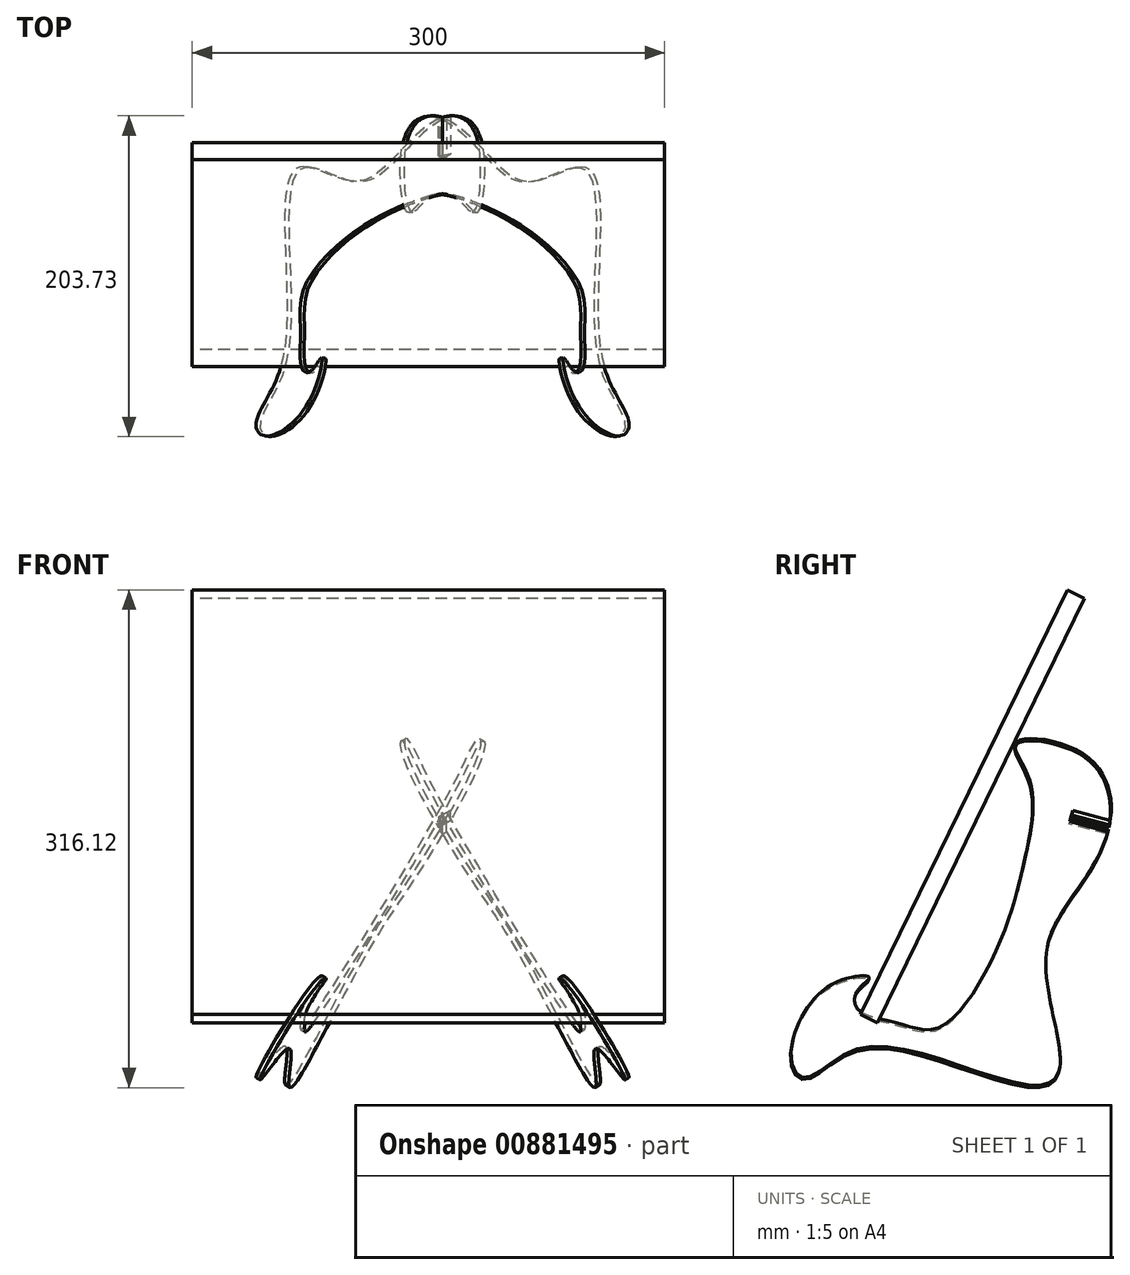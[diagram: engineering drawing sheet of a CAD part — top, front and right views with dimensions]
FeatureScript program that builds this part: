
annotation { "Feature Type Name" : "Feature", "Feature Type Description" : "" }
export const myFeature = defineFeature(function(context is Context, id is Id, definition is map)
    precondition{}
    {
        {
            var Q0;
            Q0=qCreatedBy(makeId("Front.planeOp"),FACE);
            var sketch = newSketch(context, id + "F0", { "sketchPlane" : qUnion([Q0])});
            skLineSegment(sketch, "E0.bottom", {"start": v(150, -150) * mm, "end": v(-150, -150) * mm});
            skLineSegment(sketch, "E0.top", {"start": v(150, 150) * mm, "end": v(-150, 150) * mm});
            skLineSegment(sketch, "E0.left", {"start": v(150, -150) * mm, "end": v(150, 150) * mm});
            skLineSegment(sketch, "E0.right", {"start": v(-150, -150) * mm, "end": v(-150, 150) * mm});
            skPoint(sketch, "E0.middle", {"position": v(0, 0) * mm});
            skSolve(sketch);
        }
        {
            var Q0;
            Q0 = qSketchRegion(id + "F0", true);
            extrude(context, id + "F1", {"entities" : qUnion([Q0]), "depth" : 12 * mm, "offsetDistance" : 25 * mm});
        }
        {
            var Q0;
            Q0=makeQuery(id+"F1.opExtrude","CAP_FACE",FACE,{"disambiguationData":[OSD([sQuery(id+"F0.wireOp",EDGE,"E0.bottom"),sQuery(id+"F0.wireOp",EDGE,"E0.top"),sQuery(id+"F0.wireOp",EDGE,"E0.left"),sQuery(id+"F0.wireOp",EDGE,"E0.right")])],"isStart":false});
            var sketch = newSketch(context, id + "F2", { "sketchPlane" : qUnion([Q0])});
            skLineSegment(sketch, "E1", {"start": v(-150, -150) * mm, "end": v(150, 150) * mm});
            skSolve(sketch);
        }
        {
            var Q0;
            Q0=sQuery(id+"F2.wireOp",EDGE,"E1");
            cPlane(context, id + "F3", {"entities" : qUnion([Q0]), "cplaneType" : CPlaneType.LINE_ANGLE, "offset" : 25 * mm, "angle" : 90 * degree, "width" : 150 * mm, "height" : 150 * mm});
        }
        {
            var Q0;
            Q0=makeQuery(id+"F1.opExtrude","SWEPT_BODY",BODY,{"disambiguationData":[OSD([sQuery(id+"F0.wireOp",EDGE,"E0.bottom"),sQuery(id+"F0.wireOp",EDGE,"E0.top"),sQuery(id+"F0.wireOp",EDGE,"E0.left"),sQuery(id+"F0.wireOp",EDGE,"E0.right")])]});
            var Q1;
            Q1=makeQuery(id+"F1.opExtrude","CAP_EDGE",EDGE,{"disambiguationData":[OSD([sQuery(id+"F0.wireOp",EDGE,"E0.bottom")])],"isStart":true});
            transform(context, id + "F4", {"entities" : qUnion([Q0]), "transformType" : TransformType.ROTATION, "transformAxis" : qUnion([Q1]), "angle" : 15 * degree, "makeCopy" : false});
        }
        {
            var Q0;
            Q0=qCreatedBy(makeId("Right.planeOp"),FACE);
            var sketch = newSketch(context, id + "F5", { "sketchPlane" : qUnion([Q0])});
            skFitSpline(sketch, "E2", {"points": [v(60.73, 58.65) * mm, v(102.2, 52.5) * mm, v(119.45, 8.25) * mm, v(99.15, -41.95) * mm, v(75.12, -90.56) * mm, v(79.44, -152.57) * mm, v(78.07, -183.5) * mm, v(61.93, -190.36) * mm, v(0, -172.37) * mm, v(-53.03, -169.92) * mm, v(-83.37, -190.36) * mm, v(-91.73, -177.12) * mm, v(-65.64, -123.34) * mm, v(-39.76, -115.85) * mm, v(-47.66, -126.05) * mm, v(-46.97, -140.23) * mm, v(-23.2, -148.23) * mm, v(2.9, -151.1) * mm, v(43.07, -91.63) * mm, v(63.9, -22.73) * mm, v(67.64, 32.82) * mm, v(60.73, 58.65) * mm]});
            skLineSegment(sketch, "E3", {"start": v(136.17, -190.36) * mm, "end": v(-229.05, -190.36) * mm, "construction": true});
            skSolve(sketch);
        }
        {
            var Q0;
            Q0 = qSketchRegion(id + "F5", true);
            extrude(context, id + "F6", {"entities" : qUnion([Q0]), "depth" : 3 * mm, "offsetDistance" : 25 * mm});
        }
        {
            var Q0;
            Q0=makeQuery(id+"F6.opExtrude","SWEPT_BODY",BODY,{"disambiguationData":[OSD([sQuery(id+"F5.wireOp",EDGE,"E2")])]});
            var Q1;
            Q1=makeQuery(id+"F1.opExtrude","SWEPT_EDGE",EDGE,{"disambiguationData":[OSD([sQuery(id+"F0.wireOp",EDGE,"E0.bottom"),sQuery(id+"F0.wireOp",EDGE,"E0.right")])]});
            transform(context, id + "F7", {"entities" : qUnion([Q0]), "transformType" : TransformType.ROTATION, "transformAxis" : qUnion([Q1]), "angle" : 30 * degree, "makeCopy" : false});
        }
        {
            var Q0;
            Q0=makeQuery(id+"F6.opExtrude","SWEPT_BODY",BODY,{"disambiguationData":[OSD([sQuery(id+"F5.wireOp",EDGE,"E2")])]});
            var Q1;
            Q1=qCreatedBy(makeId("Right.planeOp"),FACE);
            mirror(context, id + "F8", {"entities" : qUnion([Q0]), "mirrorPlane" : qUnion([Q1])});
        }
        {
            var Q0;
            Q0=makeQuery(id+"F8.opPattern","COPY",BODY,{"derivedFrom":makeQuery(id+"F6.opExtrude","SWEPT_BODY",BODY,{"disambiguationData":[OSD([sQuery(id+"F5.wireOp",EDGE,"E2")])]}),"instanceName":"1"});
            transform(context, id + "F9", {"entities" : qUnion([Q0]), "transformType" : TransformType.TRANSLATION_3D, "dx" : 136 * mm, "dy" : 0 * mm, "dz" : 0 * mm, "makeCopy" : false});
        }
        {
            var Q0;
            Q0=makeQuery(id+"F8.opPattern","COPY",FACE,{"derivedFrom":makeQuery(id+"F6.opExtrude","CAP_FACE",FACE,{"disambiguationData":[OSD([sQuery(id+"F5.wireOp",EDGE,"E2")])],"isStart":true}),"instanceName":"1"});
            var sketch = newSketch(context, id + "F10", { "sketchPlane" : qUnion([Q0])});
            skFitSpline(sketch, "E4", {"points": [v(41.28, -104.32) * mm, v(41.15, -105.47) * mm, v(41.02, -106.63) * mm, v(40.88, -107.78) * mm]});
            skFitSpline(sketch, "E5", {"points": [v(89.54, -119.07) * mm, v(89.78, -117.94) * mm, v(90.02, -116.81) * mm, v(90.25, -115.68) * mm]});
            skLineSegment(sketch, "E6", {"start": v(40.88, -107.78) * mm, "end": v(89.54, -119.07) * mm});
            skLineSegment(sketch, "E7", {"start": v(41.28, -104.32) * mm, "end": v(90.25, -115.68) * mm});
            skFitSpline(sketch, "E8", {"points": [v(41.28, -104.32) * mm, v(41.15, -105.47) * mm, v(41.02, -106.63) * mm, v(40.88, -107.78) * mm]});
            skFitSpline(sketch, "E9", {"points": [v(89.54, -119.07) * mm, v(89.78, -117.94) * mm, v(90.02, -116.81) * mm, v(90.25, -115.68) * mm]});
            skSolve(sketch);
        }
        {
            var Q0;
            Q0=makeQuery(id+"F8.opPattern","COPY",FACE,{"derivedFrom":makeQuery(id+"F6.opExtrude","CAP_FACE",FACE,{"disambiguationData":[OSD([sQuery(id+"F5.wireOp",EDGE,"E2")])],"isStart":false}),"instanceName":"1"});
            var sketch = newSketch(context, id + "F11", { "sketchPlane" : qUnion([Q0])});
            skLineSegment(sketch, "E10", {"start": v(-105.58, -124.57) * mm, "end": v(-64.72, -115.09) * mm});
            skLineSegment(sketch, "E11.0", {"start": v(-65.9, -110.03) * mm, "end": v(-106.95, -119.56) * mm});
            skLineSegment(sketch, "E12", {"start": v(-106.95, -119.56) * mm, "end": v(-105.58, -124.57) * mm});
            skPoint(sketch, "E13.orphan", {"position": v(-90.25, -115.68) * mm});
            skPoint(sketch, "E14.orphan", {"position": v(-89.2, -120.77) * mm});
            skLineSegment(sketch, "E15", {"start": v(-65.9, -110.03) * mm, "end": v(-64.72, -115.09) * mm});
            skSolve(sketch);
        }
        {
            var Q0;
            Q0 = qSketchRegion(id + "F11", true);
            extrude(context, id + "F12", {"entities" : qUnion([Q0]), "operationType" : NewBodyOperationType.REMOVE, "oppositeDirection" : true, "depth" : 25 * mm, "offsetDistance" : 25 * mm});
        }
        {
            var Q0;
            Q0=makeQuery(id+"F1.opExtrude","SWEPT_BODY",BODY,{"disambiguationData":[OSD([sQuery(id+"F0.wireOp",EDGE,"E0.bottom"),sQuery(id+"F0.wireOp",EDGE,"E0.top"),sQuery(id+"F0.wireOp",EDGE,"E0.left"),sQuery(id+"F0.wireOp",EDGE,"E0.right")])]});
            transform(context, id + "F13", {"entities" : qUnion([Q0]), "transformType" : TransformType.TRANSLATION_3D, "dx" : 59 * mm, "dy" : -54 * mm, "dz" : -68 * mm, "makeCopy" : false});
        }
        {
            var Q0;
            Q0=makeQuery(id+"F1.opExtrude","SWEPT_BODY",BODY,{"disambiguationData":[OSD([sQuery(id+"F0.wireOp",EDGE,"E0.bottom"),sQuery(id+"F0.wireOp",EDGE,"E0.top"),sQuery(id+"F0.wireOp",EDGE,"E0.left"),sQuery(id+"F0.wireOp",EDGE,"E0.right")])]});
            var Q1;
            Q1=makeQuery(id+"F1.opExtrude","CAP_EDGE",EDGE,{"disambiguationData":[OSD([sQuery(id+"F0.wireOp",EDGE,"E0.bottom")])],"isStart":false});
            transform(context, id + "F14", {"entities" : qUnion([Q0]), "transformType" : TransformType.ROTATION, "transformAxis" : qUnion([Q1]), "angle" : 11 * degree, "makeCopy" : false});
        }
    });
